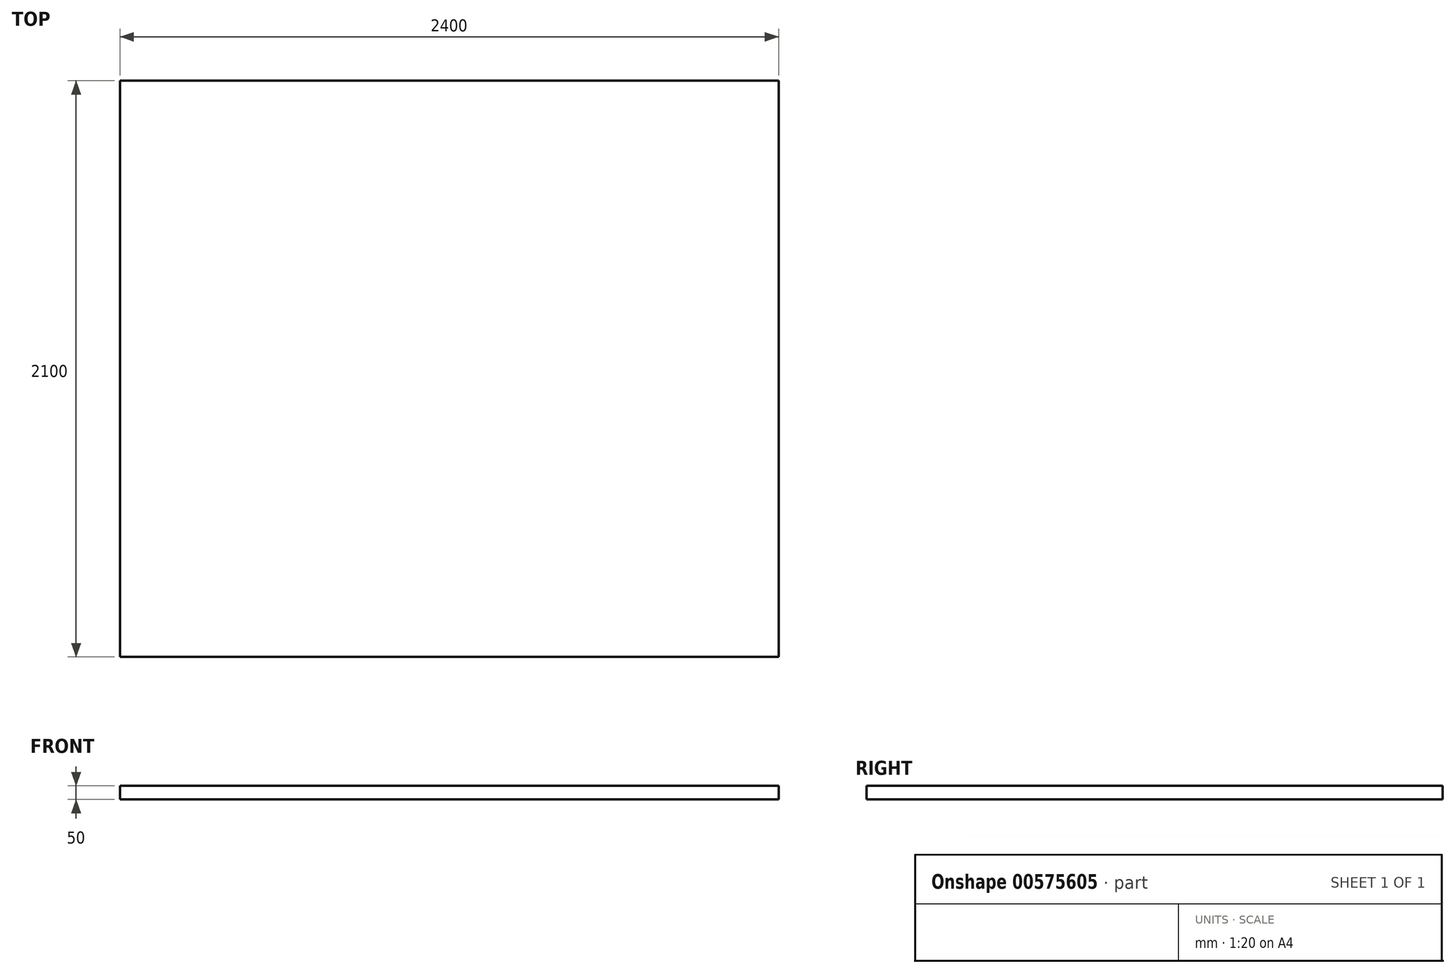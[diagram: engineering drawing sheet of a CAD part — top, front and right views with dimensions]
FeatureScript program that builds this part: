
annotation { "Feature Type Name" : "Feature", "Feature Type Description" : "" }
export const myFeature = defineFeature(function(context is Context, id is Id, definition is map)
    precondition{}
    {
        {
            var Q0;
            Q0=qCreatedBy(makeId("Top.planeOp"),FACE);
            var sketch = newSketch(context, id + "F0", { "sketchPlane" : qUnion([Q0])});
            skLineSegment(sketch, "E0.bottom", {"start": v(1200, -1050) * mm, "end": v(-1200, -1050) * mm});
            skLineSegment(sketch, "E0.top", {"start": v(1200, 1050) * mm, "end": v(-1200, 1050) * mm});
            skLineSegment(sketch, "E0.left", {"start": v(1200, -1050) * mm, "end": v(1200, 1050) * mm});
            skLineSegment(sketch, "E0.right", {"start": v(-1200, -1050) * mm, "end": v(-1200, 1050) * mm});
            skPoint(sketch, "E0.middle", {"position": v(0, 0) * mm});
            skSolve(sketch);
        }
        {
            var Q0;
            Q0 = qSketchRegion(id + "F0", true);
            extrude(context, id + "F1", {"entities" : qUnion([Q0]), "depth" : 50 * mm, "offsetDistance" : 25 * mm});
        }
    });
